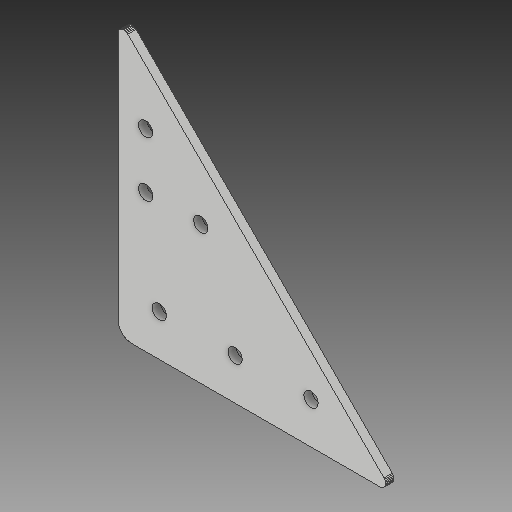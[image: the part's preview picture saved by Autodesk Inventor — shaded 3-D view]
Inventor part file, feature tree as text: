
AUTODESK INVENTOR PART (.ipt)
format: ipt  version: 2018 (Build 220112000, 112)  size: 388,608 bytes
history: native  units: mm
features: sketch x2, extrude x1, hole x1, projected_geometry x1
ambient origin geometry x8: Origin, YZ Plane, XZ Plane, XY Plane, X Axis, Y Axis, Z Axis, Center Point
bodies: Solid1 (feature_tree)
feature tree (5):
  extrude  "Extrusion1"  [1 undecoded]
  hole  "Hole1"  [1 undecoded]
  sketch  "Sketch1"  dims[d0=3.0mm d1=0.0mm]
  sketch  "Sketch2"  dims[d2=5.2mm d3=6.0mm d4=4.0mm d5=2.0mm d6=90.0deg d7=8.0mm d8=20.594885mm]
  projected_geometry  "Projected Loop1"
note: 2 required parameter values undecoded (feature->parameter linkage not recoverable at this tier; creation-order binding heuristic only, values carry confidence <= 0.55)
